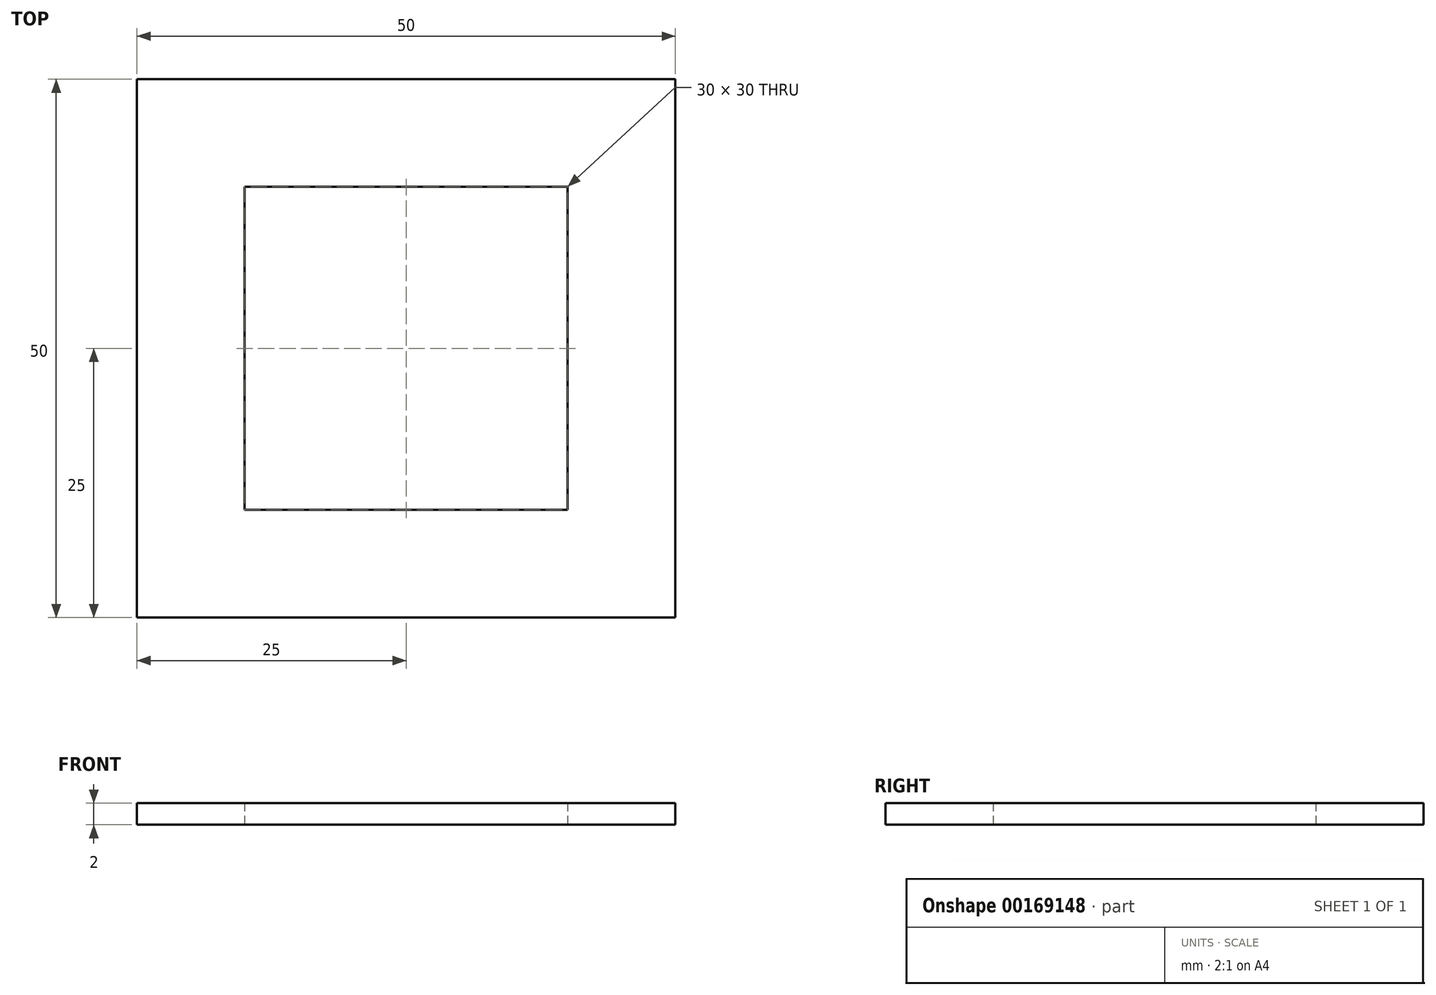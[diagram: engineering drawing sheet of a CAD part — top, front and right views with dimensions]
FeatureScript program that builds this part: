
annotation { "Feature Type Name" : "Feature", "Feature Type Description" : "" }
export const myFeature = defineFeature(function(context is Context, id is Id, definition is map)
    precondition{}
    {
        {
            var Q0;
            Q0=qCreatedBy(makeId("Top.planeOp"),FACE);
            var sketch = newSketch(context, id + "F0", { "sketchPlane" : qUnion([Q0])});
            skLineSegment(sketch, "E0.bottom", {"start": v(25, 25) * mm, "end": v(-25, 25) * mm});
            skLineSegment(sketch, "E0.top", {"start": v(25, -25) * mm, "end": v(-25, -25) * mm});
            skLineSegment(sketch, "E0.left", {"start": v(25, 25) * mm, "end": v(25, -25) * mm});
            skLineSegment(sketch, "E0.right", {"start": v(-25, 25) * mm, "end": v(-25, -25) * mm});
            skPoint(sketch, "E0.middle", {"position": v(0, 0) * mm});
            skLineSegment(sketch, "E1.0", {"start": v(15, 15) * mm, "end": v(-15, 15) * mm});
            skLineSegment(sketch, "E1.1", {"start": v(15, 15) * mm, "end": v(15, -15) * mm});
            skLineSegment(sketch, "E1.2", {"start": v(15, -15) * mm, "end": v(-15, -15) * mm});
            skLineSegment(sketch, "E1.3", {"start": v(-15, 15) * mm, "end": v(-15, -15) * mm});
            skSolve(sketch);
        }
        {
            var Q0;
            Q0=qSketchRegion(id+"F0",true);
            extrude(context, id + "F1", {"entities" : qUnion([Q0]), "depth" : 2 * mm});
        }
    });
